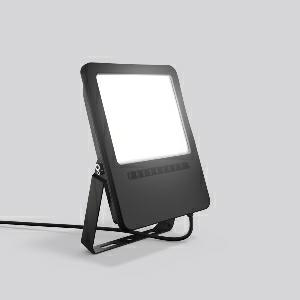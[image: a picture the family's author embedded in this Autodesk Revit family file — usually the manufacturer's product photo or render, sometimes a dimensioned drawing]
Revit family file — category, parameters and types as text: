
# Revit family: hb_450_722125_003_55fd
name_source: partatom
category: Lighting Fixtures
units: mm (PartAtom-declared; Revit-internal decimal feet)

## family parameters
Cut with Voids When Loaded = No
Host = Face
Light Source = No
Part Type = Normal
Room Calculation Point = No
Round Connector Dimension = Use Diameter
Shared = No

## types (1)
- HB 450 (1 x LED Modul 840, 7700 lm, 4000)
    Apparent Load = 70 VA
    CIE Flux Codes = 51 85 99 100 100
    Color Rendering = 80
    Color Temperature = 4000
    Default Elevation = 1800 mm
    Description = Series: HB 450
Projector for direct mains connection. Housing: die-cast aluminium, powder-coated. Bracket: steel, powder-coated. Clear glass cover. Wide flood. Pre-wired with 500 mm connection cable. 
Colour: black
Length: 360 mm
Width: 240 mm
Height: 48 mm
Lamp: LED
System power: 70 W
Rated luminous flux: 7700 lm
Luminous efficiency: 110 lm/W
Control gear: Regulated power supply
Protection class: I
Type of protection: IP 65
    Height = 48 mm  [stored 0.15748 ft]
    Lamp = 1 x LED Modul 840
    Lamp Light Flux = 7700 lm
    Lamp count = 1
    Length = 360 mm
    Lifetime = 50000 h
    Luminous efficacy = 110 lm/W
    Manufacturer = RZB
    ModVariant = No
    Model = 722125.003
    Mounting Place = Floor
    Mounting Type = Surface mounted
    Number of Poles = 1
    OnlyDefault = Yes
    Power Factor = 1
    Product Name = HB 450
    Product group = Floodlights and spotlights
    ProductGroupID = 1354
    Protection Class = Protection class I
    Protection Degree = IP 65
    RLX_Detail_Level = 1
    RLX_Emergency_Light_Flux = 0 lm
    RLX_Emergency_Type = 0
    RLX_Emergency_Type_DB = No
    RlxData = <blob elided: 27505 chars, md5=5fd80b11>
    Socket = socket
    Standby Power = 0 W
    System Light Flux = 7700 lm
    System Power = 70 W
    Type Comments = Product without accessories
    Type Image = 722125.003.jpg
    URL = http://relux.com
    VarID = ---
    Voltage = 230 V
    Voltage Range = 220-240 V
    Weight = 0.00 kg
    Width = 240 mm

note: [stored X ft] marks values corroborated as IEEE doubles in the binary element streams (Revit-internal decimal feet)

## geometry (parser evidence)
native form markers: Blend x4, Sweep x11
no freeform markers — native parametric forms only
